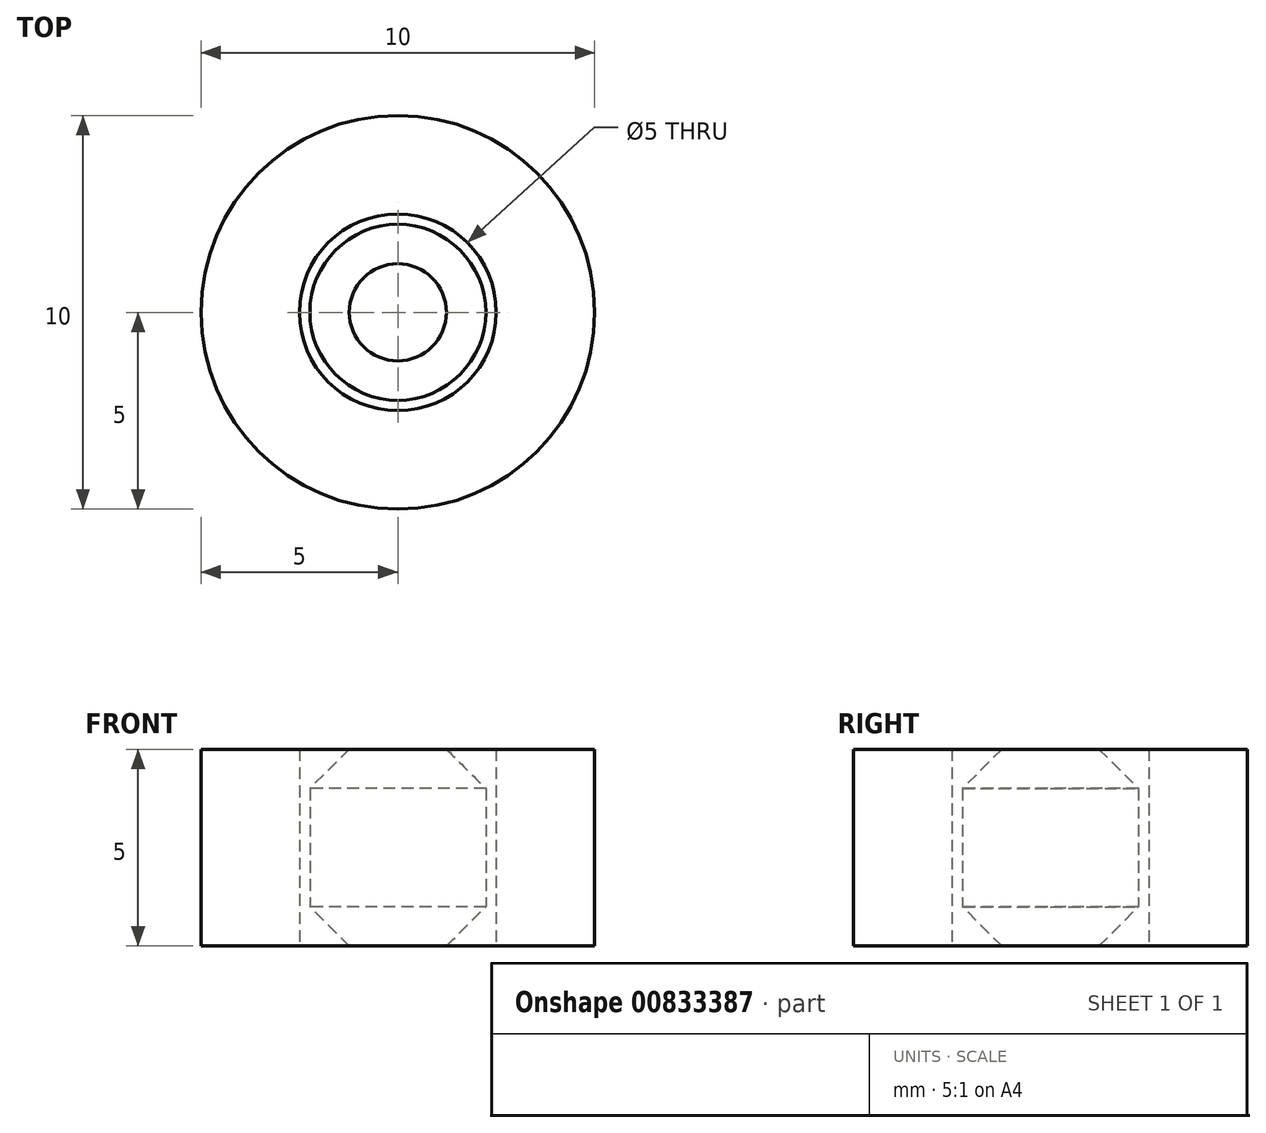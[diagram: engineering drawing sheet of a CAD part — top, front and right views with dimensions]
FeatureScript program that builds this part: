
annotation { "Feature Type Name" : "Feature", "Feature Type Description" : "" }
export const myFeature = defineFeature(function(context is Context, id is Id, definition is map)
    precondition{}
    {
        {
            var Q0;
            Q0=qCreatedBy(makeId("Top.planeOp"),FACE);
            var sketch = newSketch(context, id + "F0", { "sketchPlane" : qUnion([Q0])});
            skCircle(sketch, "E0", {"center": v(0, 0) * mm, "radius": 5 * mm});
            skCircle(sketch, "E1", {"center": v(0, 0) * mm, "radius": 2.5 * mm});
            skSolve(sketch);
        }
        {
            var Q0;
            Q0 = qSketchRegion(id + "F0", true);
            extrude(context, id + "F1", {"entities" : qUnion([Q0]), "depth" : 5 * mm, "offsetDistance" : 25 * mm});
        }
        {
            var Q0;
            Q0=qCreatedBy(makeId("Top.planeOp"),FACE);
            var sketch = newSketch(context, id + "F2", { "sketchPlane" : qUnion([Q0])});
            skCircle(sketch, "E2", {"center": v(0, 0) * mm, "radius": 2.24 * mm});
            skSolve(sketch);
        }
        {
            var Q0;
            Q0 = qSketchRegion(id + "F2", true);
            extrude(context, id + "F3", {"entities" : qUnion([Q0]), "depth" : 5 * mm, "offsetDistance" : 25 * mm});
        }
        {
            var Q0;
            Q0=makeQuery(id+"F3.opExtrude","CAP_FACE",FACE,{"disambiguationData":[OSD([sQuery(id+"F2.wireOp",EDGE,"E2")])],"isStart":true});
            var Q1;
            Q1=makeQuery(id+"F3.opExtrude","CAP_FACE",FACE,{"disambiguationData":[OSD([sQuery(id+"F2.wireOp",EDGE,"E2")])],"isStart":false});
            chamfer(context, id + "F4", {"entities" : qUnion([Q0, Q1]), "width" : 1 * mm, "tangentPropagation" : true});
        }
    });
